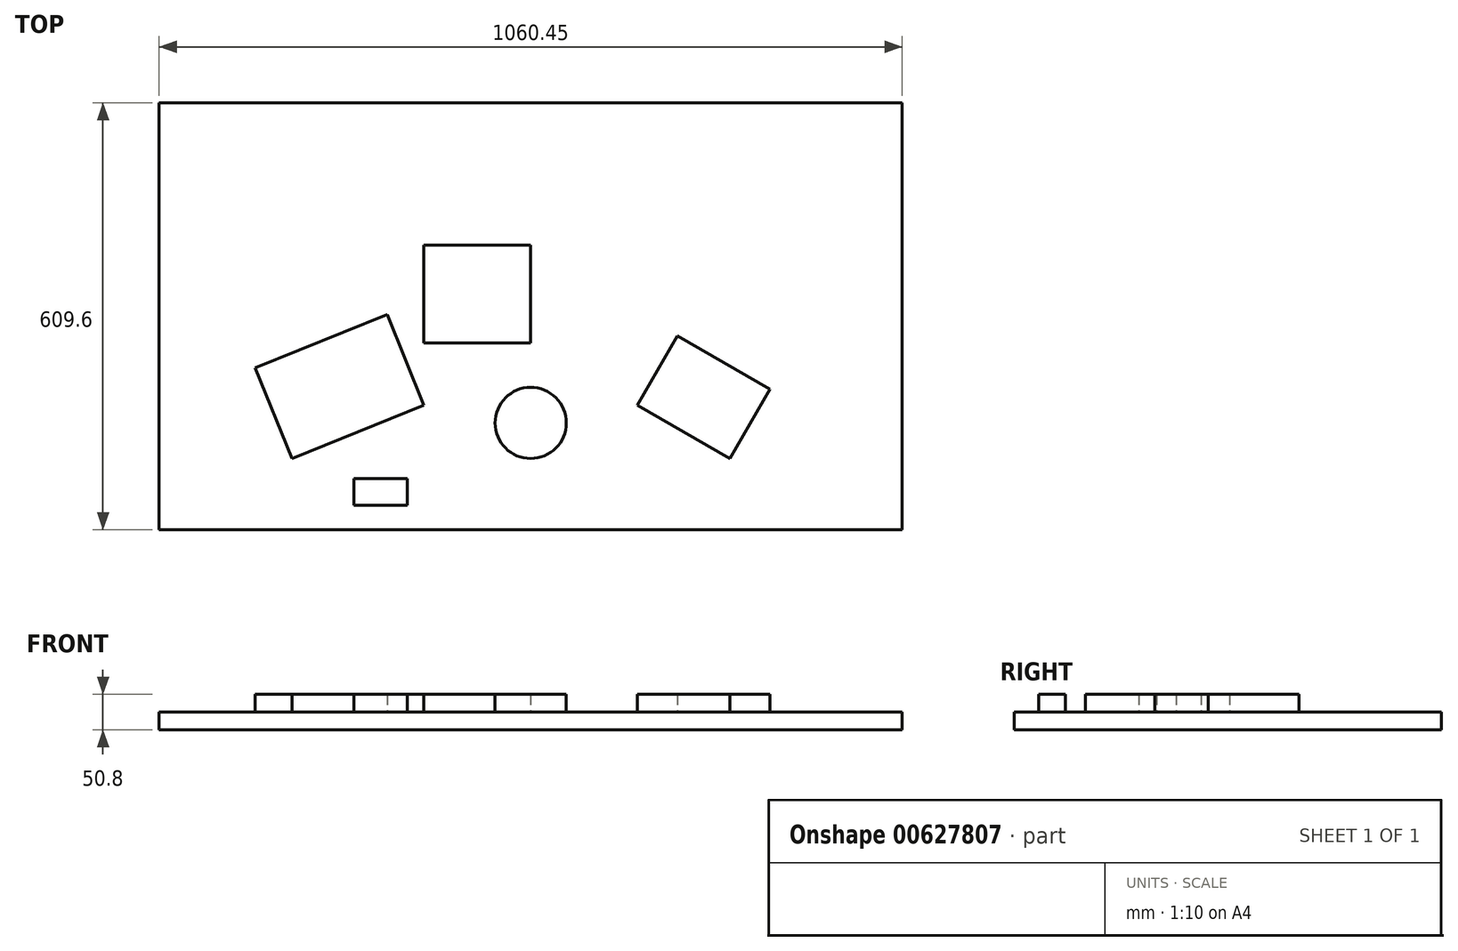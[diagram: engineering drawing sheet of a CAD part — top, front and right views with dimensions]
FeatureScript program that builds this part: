
annotation { "Feature Type Name" : "Feature", "Feature Type Description" : "" }
export const myFeature = defineFeature(function(context is Context, id is Id, definition is map)
    precondition{}
    {
        {
            var Q0;
            Q0=qCreatedBy(makeId("Top.planeOp"),FACE);
            var sketch = newSketch(context, id + "F0", { "sketchPlane" : qUnion([Q0])});
            skLineSegment(sketch, "E0.bottom", {"start": v(0.48, -0.42) * mm, "end": v(1060.93, -0.42) * mm});
            skLineSegment(sketch, "E0.top", {"start": v(0.48, 609.18) * mm, "end": v(1060.93, 609.18) * mm});
            skLineSegment(sketch, "E0.left", {"start": v(0.48, -0.42) * mm, "end": v(0.48, 609.18) * mm});
            skLineSegment(sketch, "E0.right", {"start": v(1060.93, -0.42) * mm, "end": v(1060.93, 609.18) * mm});
            skPoint(sketch, "E1", {"position": v(530.7, -0.42) * mm});
            skPoint(sketch, "E2", {"position": v(1060.93, 126.58) * mm});
            skPoint(sketch, "E3", {"position": v(1060.93, 304.38) * mm});
            skSolve(sketch);
        }
        {
            var Q0;
            Q0 = qSketchRegion(id + "F0", true);
            extrude(context, id + "F1", {"entities" : qUnion([Q0]), "oppositeDirection" : true, "depth" : 25.4 * mm, "offsetDistance" : 25.4 * mm});
        }
        {
            var Q0;
            Q0=makeQuery(id+"F1.opExtrude","CAP_FACE",FACE,{"disambiguationData":[OSD([sQuery(id+"F0.wireOp",EDGE,"E0.bottom"),sQuery(id+"F0.wireOp",EDGE,"E0.top"),sQuery(id+"F0.wireOp",EDGE,"E0.left"),sQuery(id+"F0.wireOp",EDGE,"E0.right")])],"isStart":true});
            var sketch = newSketch(context, id + "F2", { "sketchPlane" : qUnion([Q0])});
            skPoint(sketch, "E4", {"position": v(137.55, 230.69) * mm});
            skPoint(sketch, "E5", {"position": v(189.94, 101.18) * mm});
            skPoint(sketch, "E6", {"position": v(378.3, 177.38) * mm});
            skPoint(sketch, "E7", {"position": v(325.92, 306.89) * mm});
            skLineSegment(sketch, "E8", {"start": v(325.92, 306.89) * mm, "end": v(378.3, 177.38) * mm});
            skLineSegment(sketch, "E9", {"start": v(189.94, 101.18) * mm, "end": v(378.3, 177.38) * mm});
            skLineSegment(sketch, "E10", {"start": v(137.55, 230.69) * mm, "end": v(325.92, 306.89) * mm});
            skLineSegment(sketch, "E11", {"start": v(137.55, 230.69) * mm, "end": v(189.94, 101.18) * mm});
            skPoint(sketch, "E12", {"position": v(740.26, 276.37) * mm});
            skPoint(sketch, "E13", {"position": v(683.1, 177.38) * mm});
            skPoint(sketch, "E14", {"position": v(815.1, 101.18) * mm});
            skPoint(sketch, "E15", {"position": v(872.24, 200.17) * mm});
            skLineSegment(sketch, "E16", {"start": v(872.24, 200.17) * mm, "end": v(815.1, 101.18) * mm});
            skLineSegment(sketch, "E17", {"start": v(683.1, 177.38) * mm, "end": v(815.1, 101.18) * mm});
            skLineSegment(sketch, "E18", {"start": v(740.26, 276.37) * mm, "end": v(872.24, 200.17) * mm});
            skLineSegment(sketch, "E19", {"start": v(740.26, 276.37) * mm, "end": v(683.1, 177.38) * mm});
            skPoint(sketch, "E20", {"position": v(530.7, -0.42) * mm});
            skPoint(sketch, "E21", {"position": v(530.7, 151.98) * mm});
            skCircle(sketch, "E22", {"center": v(530.7, 151.98) * mm, "radius": 50.8 * mm});
            skLineSegment(sketch, "E23.bottom", {"start": v(530.7, 266.28) * mm, "end": v(378.3, 266.28) * mm});
            skLineSegment(sketch, "E23.top", {"start": v(530.7, 405.98) * mm, "end": v(378.3, 405.98) * mm});
            skLineSegment(sketch, "E23.left", {"start": v(530.7, 266.28) * mm, "end": v(530.7, 405.98) * mm});
            skLineSegment(sketch, "E23.right", {"start": v(378.3, 266.28) * mm, "end": v(378.3, 405.98) * mm});
            skPoint(sketch, "E24", {"position": v(908.53, -0.42) * mm});
            skPoint(sketch, "E25", {"position": v(972.03, -140.12) * mm});
            skPoint(sketch, "E26", {"position": v(1060.93, -140.12) * mm});
            skLineSegment(sketch, "E27", {"start": v(908.53, -0.42) * mm, "end": v(972.03, -140.12) * mm});
            skLineSegment(sketch, "E28", {"start": v(1060.93, -140.12) * mm, "end": v(1060.93, -0.42) * mm});
            skLineSegment(sketch, "E29", {"start": v(1060.93, -0.42) * mm, "end": v(1060.93, -140.12) * mm});
            skLineSegment(sketch, "E30", {"start": v(972.03, -140.12) * mm, "end": v(1060.93, -140.12) * mm});
            skLineSegment(sketch, "E31.bottom", {"start": v(278.19, 72.25) * mm, "end": v(354.39, 72.25) * mm});
            skLineSegment(sketch, "E31.top", {"start": v(278.19, 34.15) * mm, "end": v(354.39, 34.15) * mm});
            skLineSegment(sketch, "E31.left", {"start": v(278.19, 72.25) * mm, "end": v(278.19, 34.15) * mm});
            skLineSegment(sketch, "E31.right", {"start": v(354.39, 72.25) * mm, "end": v(354.39, 34.15) * mm});
            skSolve(sketch);
        }
        {
            var Q0;
            Q0 = qSketchRegion(id + "F2", true);
            extrude(context, id + "F3", {"entities" : qUnion([Q0]), "operationType" : NewBodyOperationType.ADD, "depth" : 25.4 * mm, "offsetDistance" : 25.4 * mm});
        }
    });
